# Revit family: Electronics_Commercial-Loudspeakers_Biamp_Small-Design-Loudspeaker_OVO3
name_source: partatom
category: Communication Devices
units: mm (PartAtom-declared; Revit-internal decimal feet)

## family parameters
Cut with Voids When Loaded = No
Host = Face
Maintain Annotation Orientation = No
OmniClass Number = 23.85.10.11.14.14.14
Part Type = Normal
Room Calculation Point = No
Round Connector Dimension = Use Diameter
Shared = No

## types (2) — shared parameters
Connector Description = Spring terminals; 40W / 8 or 16 Ohm
Default Elevation = 4' - 0"
Depth = 0' - 4 1/2"
Frequency response in Hz = 90-20k
Height = 0' - 6 1/2"
Impedance (ohms) = 8
Loudspeaker system = 2-way
Low impedance RMS power in watts = 20
Low impedance dynamic power in watts = 40
Manufacturer = Biamp
Max SPL 1m in dB = 97
Mounting system = Turn / Tilt bracket
Product Documentation Link = https://downloads.biamp.com
Product Page URL = https://www.biamp.com
Product data url = https://bimobject.com
SPL 1W/1m in dB = 82
Tweeter size in inch = 1
URL = https://www.biamp.com
Weight = 1.76 lbf
Width = 0' - 4 1/2"
Woofer cone material = Coated paper
Woofer size in inch = 3

## per-type parameters (varying)
| type | Description | Grill Material | Housing Material |
| OVO3 B | OVO3-B 3" Small Design Loudspeaker, Black | Biamp - Plastic - Black(Grid) | Biamp - Plastic - Black |
| OVO3 W | OVO3-W 3" Small Design Loudspeaker, White | Biamp - Plastic - White(Grid) | Biamp - Plastic - White |

note: column(s) folded — value = type name in every type: Model

## geometry (parser evidence)
native form markers: Sweep x4
no freeform markers — native parametric forms only
